# Revit family: FEST-SERIES
name_source: partatom
category: Communication Devices
revit_build: Autodesk Revit 2014 (Build: 20140709_2115(x64)
units: mm (PartAtom-declared; Revit-internal decimal feet)

## types (3) — shared parameters
Baffle Material = <By Category>
Body Material = Default
Color = <By Category>
Default Elevation = 48 "
Enclosure Material = <By Category>
Family Code (default) = LOUD SPEAKER ENCLOSURES
Family Version = 2017-01
Grill Material = <By Category>
Horizontal Symmetry = Yes
IQ Category = AUDIO VISUAL INTERCOMS
Manufacturer = ATLAS SOUND
Manufacturer URL = https://www.atlasied.com
Market = Commercial, Higher Education, Emergency
MasterFormat = 27 41 13
MaterFormat Title = AUDIO VISUAL ENCLOSURES
Mount Material = Default
OmniClass Number = 23-37 17 13 19
OmniClass Title = AUDIO VISUAL ENCLOSURES
Product Documentation Link = https://www.atlasied.com
Product Page URL = https://www.atlasied.com
ScheduleType |RF| = AtlasIED Master
URL = www.atlassound.com
Vertical Symmetry = Yes
Warranty = 1 Year
zero-valued in all types: Cost, Cost MSRP, Weight in Pounds

## per-type parameters (varying)
| type | Body Spacing | Bracket Spacing | Depth | Description | Height | Model | Width |
| FEST-18S | 10.63 " | 15.5 " | 10.63 " | FLUSH MOUNT ENCLOSURE IS DESIGNED FOR USE ONLY WITH ATLAS SOUND LOUDSPEAKER SYSTEM MODELS I8SC, I8SCH, AND I8SCM. THE UNIT INCLUDES A SLOT STYLE MOUNTING SYSTEM TO ACCOMMODATE MOST ANY MATERIAL THICKNESS. THE ENCLOSURE IS CONSTRUCTED OF 20-GAUGE CRS AND FINISHED IN TEXTURED WHITE EPOXY. | 3.75 " | FEST-I8S | 17.63 " |
| FEST-18SC | 11.59 " | 16.5 " | 13.13 " | FLUSH MOUNT ENCLOSURE IS DESIGNED FOR USE ONLY WITH ATLAS SOUND LOUDSPEAKER SYSTEM MODELS I8S AND I8SM. THE UNIT INCLUDES A SLOT STYLE MOUNTING SYSTEM TO ACCOMMODATE ALMOST ANY MATERIAL THICKNESS. THE ENCLOSURE IS CONSTRUCTED OF 20-GAUGE CRS AND FINISHED IN RECLAIMED POWDER COAT FINISH. | 4 " | FEST-I8SC | 18.63 " |
| FEST-IH | 9.63 " | 14.5 " | 9.63 " | FLUSH MOUNT STAINLESS STEEL ENCLOSURE IS DESIGNED FOR USE ONLY WITH ATLAS SOUND LOUDSPEAKER SYSTEM MODEL IHVP. EXTERNAL MOUNTING WINGS ALLOW FOR EASY INSTALLATION INTO STUD MATERIAL. THE ENCLOSURE IS CONSTRUCTED OF 18-GAUGE STAINLESS STEEL. | 6 " | FEST-IH | 16.63 " |

## geometry (parser evidence)
native form markers: Blend x12, Sweep x2
no freeform markers — native parametric forms only
